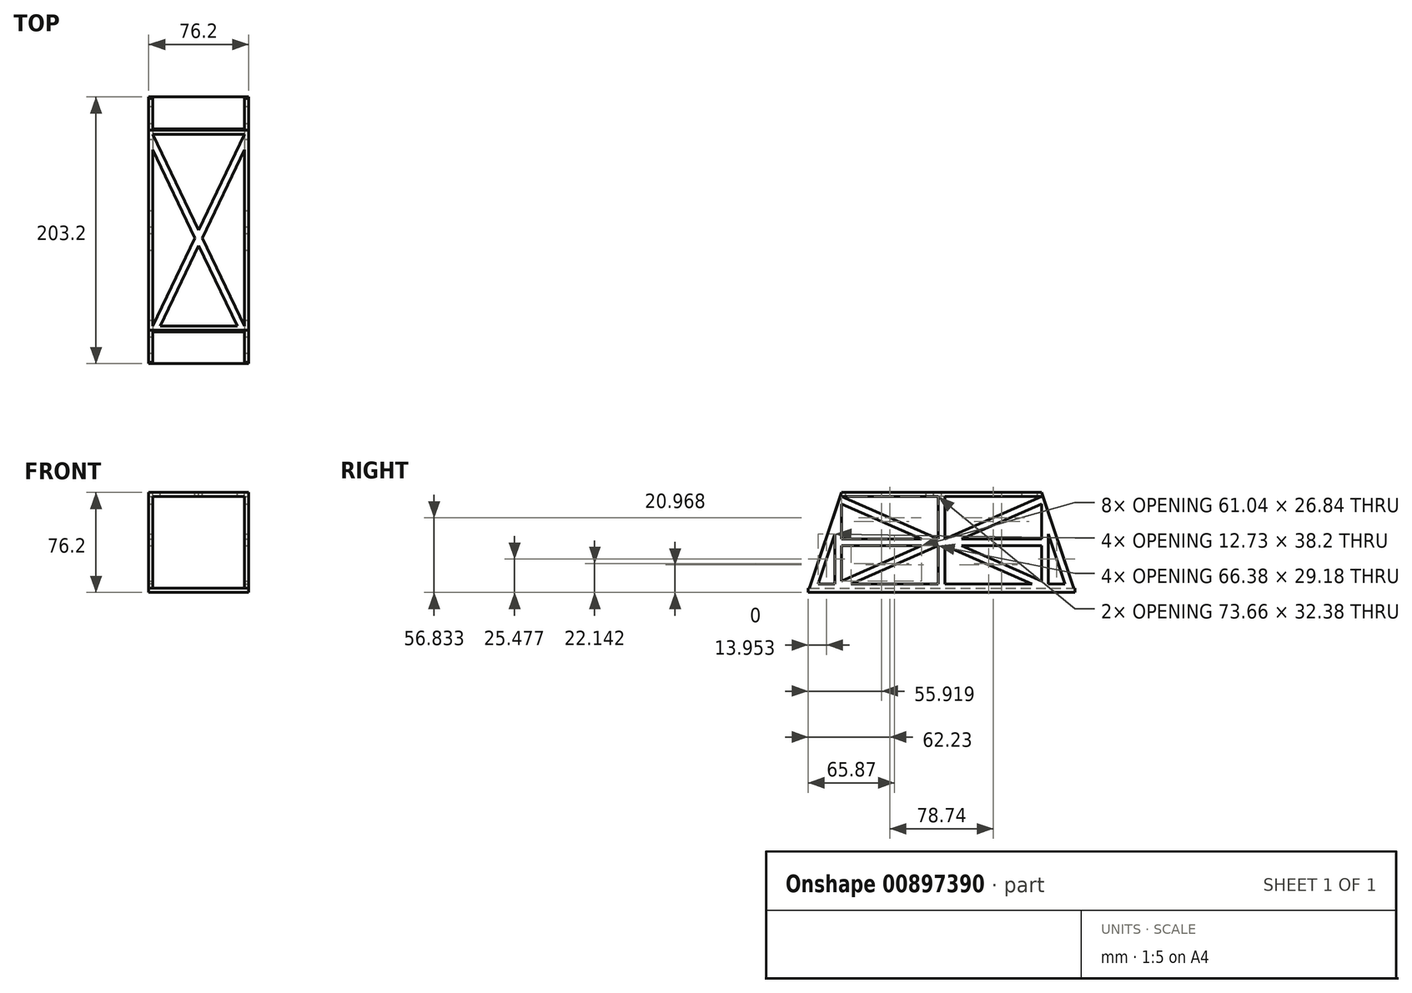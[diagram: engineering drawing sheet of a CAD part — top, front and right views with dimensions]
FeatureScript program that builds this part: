
annotation { "Feature Type Name" : "Feature", "Feature Type Description" : "" }
export const myFeature = defineFeature(function(context is Context, id is Id, definition is map)
    precondition{}
    {
        {
            var Q0;
            Q0=qCreatedBy(makeId("Right.planeOp"),FACE);
            var sketch = newSketch(context, id + "F0", { "sketchPlane" : qUnion([Q0])});
            skLineSegment(sketch, "E0", {"start": v(-101.6, -38.1) * mm, "end": v(101.6, -38.1) * mm});
            skLineSegment(sketch, "E1", {"start": v(-76.2, 38.1) * mm, "end": v(76.2, 38.1) * mm});
            skLineSegment(sketch, "E2", {"start": v(-76.2, 38.1) * mm, "end": v(-101.6, -38.1) * mm});
            skLineSegment(sketch, "E3", {"start": v(76.2, 38.1) * mm, "end": v(101.6, -38.1) * mm});
            skSolve(sketch);
        }
        {
            var Q0;
            Q0=makeQuery(id+"F0.imprint","IMPRINT",FACE,{"disambiguationData":[TD([[makeQuery(id+"F0.imprint","IMPRINT",EDGE,{"derivedFrom":sQuery(id+"F0.wireOp",EDGE,"E0")}),1.0]])]});
            extrude(context, id + "F1", {"entities" : qUnion([Q0]), "endBound" : BoundingType.SYMMETRIC, "depth" : 76.2 * mm, "offsetDistance" : 25.4 * mm});
        }
        {
            var Q0;
            Q0=makeQuery(id+"F1.opExtrude","CAP_FACE",FACE,{"disambiguationData":[OSD([sQuery(id+"F0.wireOp",EDGE,"E0"),sQuery(id+"F0.wireOp",EDGE,"E1"),sQuery(id+"F0.wireOp",EDGE,"E2"),sQuery(id+"F0.wireOp",EDGE,"E3")])],"isStart":false});
            var sketch = newSketch(context, id + "F2", { "sketchPlane" : qUnion([Q0])});
            skLineSegment(sketch, "E4.bottom", {"start": v(76.2, -34.92) * mm, "end": v(-76.2, -34.92) * mm});
            skLineSegment(sketch, "E4.top", {"start": v(76.2, 34.92) * mm, "end": v(-76.2, 34.92) * mm});
            skLineSegment(sketch, "E4.left", {"start": v(76.2, -34.92) * mm, "end": v(76.2, 34.92) * mm});
            skLineSegment(sketch, "E4.right", {"start": v(-76.2, -34.92) * mm, "end": v(-76.2, 34.92) * mm});
            skPoint(sketch, "E4.middle", {"position": v(0, 0) * mm});
            skLineSegment(sketch, "E5.bottom", {"start": v(2.54, -34.92) * mm, "end": v(-2.54, -34.92) * mm});
            skLineSegment(sketch, "E5.top", {"start": v(2.54, 34.92) * mm, "end": v(-2.54, 34.92) * mm});
            skLineSegment(sketch, "E5.left", {"start": v(2.54, -34.93) * mm, "end": v(2.54, 34.93) * mm});
            skLineSegment(sketch, "E5.right", {"start": v(-2.54, -34.93) * mm, "end": v(-2.54, 34.93) * mm});
            skLineSegment(sketch, "E6", {"start": v(-2.54, 0) * mm, "end": v(2.54, 0) * mm});
            skLineSegment(sketch, "E7.bottom", {"start": v(76.2, -2.54) * mm, "end": v(-76.2, -2.54) * mm});
            skLineSegment(sketch, "E7.top", {"start": v(76.2, 2.54) * mm, "end": v(-76.2, 2.54) * mm});
            skLineSegment(sketch, "E7.left", {"start": v(76.2, -2.54) * mm, "end": v(76.2, 2.54) * mm});
            skLineSegment(sketch, "E7.right", {"start": v(-76.2, -2.54) * mm, "end": v(-76.2, 2.54) * mm});
            skLineSegment(sketch, "E8", {"start": v(-76.2, 34.92) * mm, "end": v(-2.54, 2.54) * mm});
            skLineSegment(sketch, "E9", {"start": v(2.54, 2.54) * mm, "end": v(76.2, 34.92) * mm});
            skLineSegment(sketch, "E10", {"start": v(2.54, -2.54) * mm, "end": v(76.2, -34.92) * mm});
            skLineSegment(sketch, "E11", {"start": v(-2.54, -2.54) * mm, "end": v(-76.2, -34.92) * mm});
            skLineSegment(sketch, "E12", {"start": v(-76.2, -29.38) * mm, "end": v(-15.16, -2.54) * mm});
            skLineSegment(sketch, "E13", {"start": v(-15.16, 2.54) * mm, "end": v(-76.2, 29.38) * mm});
            skLineSegment(sketch, "E14", {"start": v(15.16, 2.54) * mm, "end": v(76.2, 29.38) * mm});
            skLineSegment(sketch, "E15", {"start": v(15.16, -2.54) * mm, "end": v(76.2, -29.38) * mm});
            skLineSegment(sketch, "E16", {"start": v(-81.28, -34.92) * mm, "end": v(-81.28, 6.48) * mm});
            skLineSegment(sketch, "E17", {"start": v(-81.28, 6.48) * mm, "end": v(-95.08, -34.92) * mm});
            skLineSegment(sketch, "E18", {"start": v(-95.08, -34.92) * mm, "end": v(-81.28, -34.92) * mm});
            skLineSegment(sketch, "E19.MirrorCS", {"start": v(81.28, -34.92) * mm, "end": v(81.28, 6.48) * mm});
            skLineSegment(sketch, "E20.MirrorCS", {"start": v(81.28, 6.48) * mm, "end": v(95.08, -34.92) * mm});
            skLineSegment(sketch, "E21.MirrorCS", {"start": v(95.08, -34.92) * mm, "end": v(81.28, -34.92) * mm});
            skSolve(sketch);
        }
        {
            var Q0;
            Q0=qCreatedBy(makeId("Front.planeOp"),FACE);
            var sketch = newSketch(context, id + "F3", { "sketchPlane" : qUnion([Q0])});
            skLineSegment(sketch, "E22.bottom", {"start": v(-34.93, -34.93) * mm, "end": v(34.93, -34.93) * mm});
            skLineSegment(sketch, "E22.top", {"start": v(-34.93, 34.93) * mm, "end": v(34.93, 34.93) * mm});
            skLineSegment(sketch, "E22.left", {"start": v(-34.93, -34.93) * mm, "end": v(-34.93, 34.93) * mm});
            skLineSegment(sketch, "E22.right", {"start": v(34.92, -34.93) * mm, "end": v(34.92, 34.93) * mm});
            skPoint(sketch, "E22.middle", {"position": v(0, 0) * mm});
            skSolve(sketch);
        }
        {
            var Q0;
            Q0 = qSketchRegion(id + "F3", true);
            extrude(context, id + "F4", {"entities" : qUnion([Q0]), "operationType" : NewBodyOperationType.REMOVE, "endBound" : BoundingType.SYMMETRIC, "depth" : 254 * mm, "offsetDistance" : 25.4 * mm});
        }
        {
            var Q0;
            Q0=makeQuery(id+"F2.imprint","IMPRINT",FACE,{"disambiguationData":[TD([[makeQuery(id+"F2.imprint","IMPRINT",EDGE,{"derivedFrom":sQuery(id+"F2.wireOp",EDGE,"E16")}),1.0]])]});
            var Q1;
            {var subQ3=sQuery(id+"F2.wireOp",EDGE,"E12");Q1=makeQuery(id+"F2.imprint","IMPRINT",FACE,{"disambiguationData":[TD([[makeQuery(id+"F2.imprint","IMPRINT",EDGE,{"derivedFrom":subQ3}),1.0]])]});}
            var Q2;
            {var subQ3=sQuery(id+"F2.wireOp",EDGE,"E13");Q2=makeQuery(id+"F2.imprint","IMPRINT",FACE,{"disambiguationData":[TD([[makeQuery(id+"F2.imprint","IMPRINT",EDGE,{"derivedFrom":subQ3}),1.0]])]});}
            var Q3;
            {var subQ0=sQuery(id+"F2.wireOp",EDGE,"E8");Q3=makeQuery(id+"F2.imprint","IMPRINT",FACE,{"disambiguationData":[TD([[makeQuery(id+"F2.imprint","IMPRINT",EDGE,{"derivedFrom":subQ0}),1.0]])]});}
            var Q4;
            {var subQ0=sQuery(id+"F2.wireOp",EDGE,"E9");Q4=makeQuery(id+"F2.imprint","IMPRINT",FACE,{"disambiguationData":[TD([[makeQuery(id+"F2.imprint","IMPRINT",EDGE,{"derivedFrom":subQ0}),1.0]])]});}
            var Q5;
            {var subQ3=sQuery(id+"F2.wireOp",EDGE,"E14");Q5=makeQuery(id+"F2.imprint","IMPRINT",FACE,{"disambiguationData":[TD([[makeQuery(id+"F2.imprint","IMPRINT",EDGE,{"derivedFrom":subQ3}),-1.0]])]});}
            var Q6;
            {var subQ3=sQuery(id+"F2.wireOp",EDGE,"E15");Q6=makeQuery(id+"F2.imprint","IMPRINT",FACE,{"disambiguationData":[TD([[makeQuery(id+"F2.imprint","IMPRINT",EDGE,{"derivedFrom":subQ3}),1.0]])]});}
            var Q7;
            {var subQ0=sQuery(id+"F2.wireOp",EDGE,"E10");Q7=makeQuery(id+"F2.imprint","IMPRINT",FACE,{"disambiguationData":[TD([[makeQuery(id+"F2.imprint","IMPRINT",EDGE,{"derivedFrom":subQ0}),-1.0]])]});}
            var Q8;
            Q8=makeQuery(id+"F2.imprint","IMPRINT",FACE,{"disambiguationData":[TD([[makeQuery(id+"F2.imprint","IMPRINT",EDGE,{"derivedFrom":sQuery(id+"F2.wireOp",EDGE,"E19.MirrorCS")}),-1.0]])]});
            var Q9;
            {var subQ0=sQuery(id+"F2.wireOp",EDGE,"E11");Q9=makeQuery(id+"F2.imprint","IMPRINT",FACE,{"disambiguationData":[TD([[makeQuery(id+"F2.imprint","IMPRINT",EDGE,{"derivedFrom":subQ0}),1.0]])]});}
            extrude(context, id + "F5", {"entities" : qUnion([Q0, Q1, Q2, Q3, Q4, Q5, Q6, Q7, Q8, Q9]), "operationType" : NewBodyOperationType.REMOVE, "oppositeDirection" : true, "depth" : 76.2 * mm, "offsetDistance" : 25.4 * mm});
        }
        {
            var Q0;
            Q0=makeQuery(id+"F1.opExtrude","SWEPT_FACE",FACE,{"disambiguationData":[OSD([sQuery(id+"F0.wireOp",EDGE,"E1")])]});
            var sketch = newSketch(context, id + "F6", { "sketchPlane" : qUnion([Q0])});
            skLineSegment(sketch, "E23.bottom", {"start": v(34.92, -73.02) * mm, "end": v(-34.92, -73.02) * mm});
            skLineSegment(sketch, "E23.top", {"start": v(34.92, 73.02) * mm, "end": v(-34.92, 73.02) * mm});
            skLineSegment(sketch, "E23.left", {"start": v(-34.92, -73.02) * mm, "end": v(-34.92, 73.02) * mm});
            skLineSegment(sketch, "E23.right", {"start": v(34.92, -73.02) * mm, "end": v(34.92, 73.02) * mm});
            skPoint(sketch, "E23.middle", {"position": v(0, 0) * mm});
            skLineSegment(sketch, "E24", {"start": v(-34.92, 73.02) * mm, "end": v(34.92, -73.02) * mm});
            skLineSegment(sketch, "E25", {"start": v(34.92, 73.02) * mm, "end": v(-34.92, -73.02) * mm});
            skLineSegment(sketch, "E26", {"start": v(-34.93, 61.25) * mm, "end": v(29.3, -73.02) * mm});
            skLineSegment(sketch, "E27", {"start": v(34.92, 61.25) * mm, "end": v(-29.3, -73.02) * mm});
            skSolve(sketch);
        }
        {
            var Q0;
            {var subQ0=sQuery(id+"F6.wireOp",EDGE,"E23.top");Q0=makeQuery(id+"F6.imprint","IMPRINT",FACE,{"disambiguationData":[TD([[makeQuery(id+"F6.imprint","IMPRINT",EDGE,{"derivedFrom":subQ0}),1.0]])]});}
            var Q1;
            {var subQ1=sQuery(id+"F6.wireOp",EDGE,"E23.left");var subQ3=sQuery(id+"F6.wireOp",EDGE,"E26");var subQ4=makeQuery(id+"F6.imprint","INTERSECT",VERTEX,{"derivedFrom":[subQ1,subQ3]});Q1=makeQuery(id+"F6.imprint","IMPRINT",FACE,{"disambiguationData":[TD([[makeQuery(id+"F6.imprint","IMPRINT",EDGE,{"disambiguationData":[TD([[subQ4,-1.0]])],"derivedFrom":subQ3}),-1.0]])]});}
            var Q2;
            {var subQ1=sQuery(id+"F6.wireOp",EDGE,"E23.right");var subQ3=sQuery(id+"F6.wireOp",EDGE,"E27");var subQ4=makeQuery(id+"F6.imprint","INTERSECT",VERTEX,{"derivedFrom":[subQ1,subQ3]});Q2=makeQuery(id+"F6.imprint","IMPRINT",FACE,{"disambiguationData":[TD([[makeQuery(id+"F6.imprint","IMPRINT",EDGE,{"disambiguationData":[TD([[subQ4,-1.0]])],"derivedFrom":subQ3}),1.0]])]});}
            var Q3;
            {var subQ0=sQuery(id+"F6.wireOp",EDGE,"E26");var subQ1=sQuery(id+"F6.wireOp",EDGE,"E23.bottom");var subQ2=makeQuery(id+"F6.imprint","INTERSECT",VERTEX,{"derivedFrom":[subQ1,subQ0]});Q3=makeQuery(id+"F6.imprint","IMPRINT",FACE,{"disambiguationData":[TD([[makeQuery(id+"F6.imprint","IMPRINT",EDGE,{"disambiguationData":[TD([[subQ2,-1.0]])],"derivedFrom":subQ1}),-1.0]])]});}
            extrude(context, id + "F7", {"entities" : qUnion([Q0, Q1, Q2, Q3]), "operationType" : NewBodyOperationType.REMOVE, "oppositeDirection" : true, "depth" : 3.17 * mm, "offsetDistance" : 25.4 * mm});
        }
        {
            var Q0;
            Q0=makeQuery(id+"F1.opExtrude","CAP_FACE",FACE,{"disambiguationData":[OSD([sQuery(id+"F0.wireOp",EDGE,"E0"),sQuery(id+"F0.wireOp",EDGE,"E1"),sQuery(id+"F0.wireOp",EDGE,"E2"),sQuery(id+"F0.wireOp",EDGE,"E3")])],"isStart":false});
            var sketch = newSketch(context, id + "F8", { "sketchPlane" : qUnion([Q0])});
            skLineSegment(sketch, "E28.bottom", {"start": v(-101.6, -38.1) * mm, "end": v(-95.08, -38.1) * mm});
            skLineSegment(sketch, "E28.top", {"start": v(-101.6, -34.92) * mm, "end": v(-95.08, -34.92) * mm});
            skLineSegment(sketch, "E28.left", {"start": v(-101.6, -38.1) * mm, "end": v(-101.6, -34.92) * mm});
            skLineSegment(sketch, "E28.right", {"start": v(-95.08, -38.1) * mm, "end": v(-95.08, -34.92) * mm});
            skLineSegment(sketch, "E29.MirrorCS", {"start": v(101.6, -34.92) * mm, "end": v(95.08, -34.92) * mm});
            skLineSegment(sketch, "E30.MirrorCS", {"start": v(95.08, -38.1) * mm, "end": v(95.08, -34.92) * mm});
            skLineSegment(sketch, "E31.MirrorCS", {"start": v(101.6, -38.1) * mm, "end": v(95.08, -38.1) * mm});
            skLineSegment(sketch, "E32.MirrorCS", {"start": v(101.6, -38.1) * mm, "end": v(101.6, -34.92) * mm});
            skSolve(sketch);
        }
        {
            var Q0;
            Q0 = qSketchRegion(id + "F8", true);
            extrude(context, id + "F9", {"entities" : qUnion([Q0]), "operationType" : NewBodyOperationType.ADD, "oppositeDirection" : true, "depth" : 76.2 * mm, "offsetDistance" : 25.4 * mm});
        }
        {
            var Q0;
            {var subQ0=sQuery(id+"F2.wireOp",EDGE,"E4.bottom");Q0=makeQuery(id+"F9.boolean.opBoolean","MERGE",FACE,{"derivedFrom":[makeQuery(id+"F5.boolean.opBoolean","MERGE",FACE,{"derivedFrom":[makeQuery(id+"F4.boolean.opBoolean","COPY",FACE,{"derivedFrom":makeQuery(id+"F4.opExtrude","SWEPT_FACE",FACE,{"disambiguationData":[OSD([sQuery(id+"F3.wireOp",EDGE,"E22.bottom")])]})})],"fromTools":[makeQuery(id+"F5.opExtrude","SWEPT_FACE",FACE,{"disambiguationData":[OSD([subQ0]),TDD([makeQuery(id+"F2.imprint","IMPRINT",EDGE,{"disambiguationData":[TD([[makeQuery(id+"F2.imprint","INTERSECT",VERTEX,{"derivedFrom":[subQ0,sQuery(id+"F2.wireOp",EDGE,"E4.left"),sQuery(id+"F2.wireOp",EDGE,"E10")]}),-1.0]])],"derivedFrom":subQ0})])]}),makeQuery(id+"F5.opExtrude","SWEPT_FACE",FACE,{"disambiguationData":[OSD([subQ0]),TDD([makeQuery(id+"F2.imprint","IMPRINT",EDGE,{"disambiguationData":[TD([[makeQuery(id+"F2.imprint","INTERSECT",VERTEX,{"derivedFrom":[subQ0,sQuery(id+"F2.wireOp",EDGE,"E4.right"),sQuery(id+"F2.wireOp",EDGE,"E11")]}),1.0]])],"derivedFrom":subQ0})])]}),makeQuery(id+"F5.opExtrude","SWEPT_FACE",FACE,{"disambiguationData":[OSD([sQuery(id+"F2.wireOp",EDGE,"E18")])]}),makeQuery(id+"F5.opExtrude","SWEPT_FACE",FACE,{"disambiguationData":[OSD([sQuery(id+"F2.wireOp",EDGE,"E21.MirrorCS")])]})]}),makeQuery(id+"F9.opExtrude","SWEPT_FACE",FACE,{"disambiguationData":[OSD([sQuery(id+"F8.wireOp",EDGE,"E28.top")])]}),makeQuery(id+"F9.opExtrude","SWEPT_FACE",FACE,{"disambiguationData":[OSD([sQuery(id+"F8.wireOp",EDGE,"E29.MirrorCS")])]})]});}
            var sketch = newSketch(context, id + "F10", { "sketchPlane" : qUnion([Q0])});
            skLineSegment(sketch, "E33.bottom", {"start": v(34.92, 95.08) * mm, "end": v(38.1, 95.08) * mm});
            skLineSegment(sketch, "E33.top", {"start": v(34.92, -95.08) * mm, "end": v(38.1, -95.08) * mm});
            skLineSegment(sketch, "E33.left", {"start": v(34.92, 95.08) * mm, "end": v(34.92, -95.08) * mm});
            skLineSegment(sketch, "E33.right", {"start": v(38.1, 95.08) * mm, "end": v(38.1, -95.08) * mm});
            skLineSegment(sketch, "E34.MirrorCS", {"start": v(-38.1, 95.08) * mm, "end": v(-38.1, -95.08) * mm});
            skLineSegment(sketch, "E35.MirrorCS", {"start": v(-34.92, 95.08) * mm, "end": v(-34.92, -95.08) * mm});
            skLineSegment(sketch, "E36", {"start": v(-38.1, -95.08) * mm, "end": v(-34.92, -95.08) * mm});
            skLineSegment(sketch, "E37", {"start": v(-38.1, 95.08) * mm, "end": v(-34.92, 95.08) * mm});
            skSolve(sketch);
        }
        {
            var Q0;
            Q0 = qSketchRegion(id + "F10", true);
            extrude(context, id + "F11", {"entities" : qUnion([Q0]), "operationType" : NewBodyOperationType.ADD, "depth" : 3.17 * mm, "offsetDistance" : 25.4 * mm});
        }
        {
            var Q0;
            Q0 = qSketchRegion(id + "F10", true);
            extrude(context, id + "F12", {"entities" : qUnion([Q0]), "operationType" : NewBodyOperationType.ADD, "depth" : 3.2 * mm, "offsetDistance" : 25.4 * mm});
        }
    });
